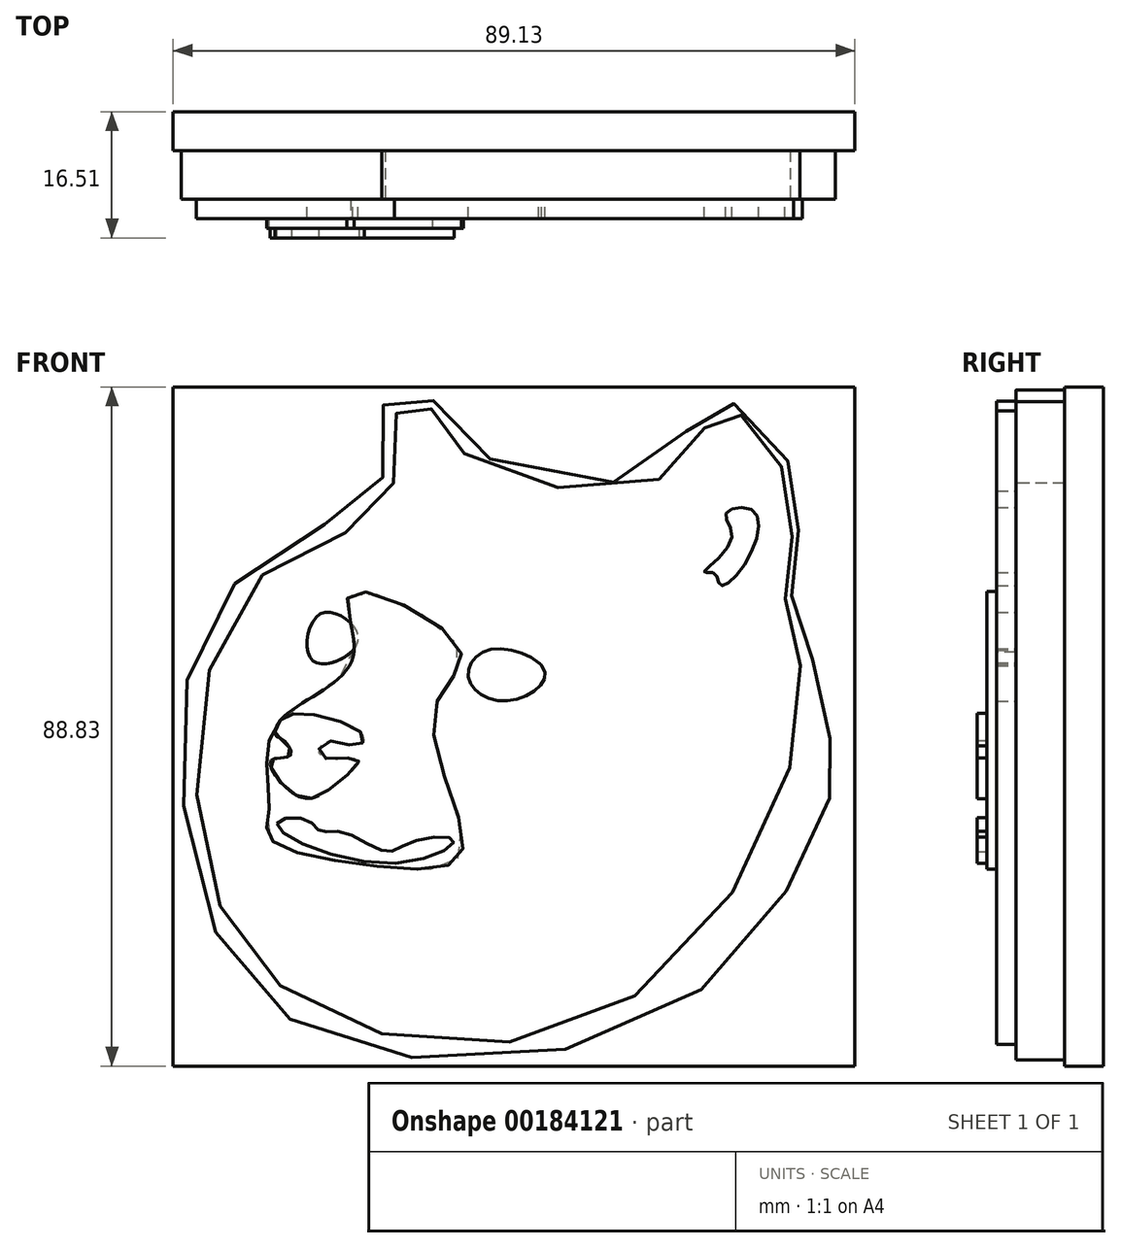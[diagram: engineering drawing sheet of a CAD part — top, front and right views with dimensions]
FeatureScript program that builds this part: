
annotation { "Feature Type Name" : "Feature", "Feature Type Description" : "" }
export const myFeature = defineFeature(function(context is Context, id is Id, definition is map)
    precondition{}
    {
        {
            var Q0;
            Q0=qCreatedBy(makeId("Front.planeOp"),FACE);
            var sketch = newSketch(context, id + "F0", { "sketchPlane" : qUnion([Q0])});
            skFitSpline(sketch, "E0", {"points": [v(14.94, 45.02) * mm, v(22.2, 53.36) * mm, v(26.38, 52.96) * mm, v(32.43, 41.52) * mm, v(31.36, 30.35) * mm, v(33.65, 16.35) * mm, v(11.17, -22.95) * mm, v(-29.47, -24.43) * mm, v(-44.95, -1.95) * mm, v(-37.01, 32.5) * mm, v(-20.6, 42.06) * mm, v(-19.11, 54.3) * mm, v(-15.34, 54.7) * mm, v(-10.63, 48.52) * mm, v(14.94, 45.02) * mm]});
            skFitSpline(sketch, "E1", {"points": [v(-29.31, 27.45) * mm, v(-24.63, 25.16) * mm, v(-26.06, 21.88) * mm, v(-30.59, 21.6) * mm, v(-29.31, 27.45) * mm]});
            skFitSpline(sketch, "E2", {"points": [v(-9.97, 18.96) * mm, v(-7.16, 22.78) * mm, v(0, 19.76) * mm, v(-4.88, 16.08) * mm, v(-9.97, 18.96) * mm]});
            skFitSpline(sketch, "E3", {"points": [v(23.71, 40.6) * mm, v(24.4, 37.2) * mm, v(20.85, 32.88) * mm, v(22.16, 32.77) * mm, v(22.95, 31.2) * mm, v(26.4, 34.37) * mm, v(27.23, 40.97) * mm, v(23.71, 40.6) * mm]});
            skFitSpline(sketch, "E4", {"points": [v(-0.44, 20.64) * mm, v(-3.05, 17.42) * mm, v(-6.06, 17.5) * mm, v(-6.22, 20.9) * mm, v(-2.1, 21.23) * mm, v(-0.44, 20.64) * mm]});
            skFitSpline(sketch, "E5", {"points": [v(-28.4, 26.53) * mm, v(-25.3, 26.14) * mm, v(-25.11, 22.7) * mm, v(-29.2, 21.88) * mm, v(-28.4, 26.53) * mm]});
            skSolve(sketch);
        }
        {
            var Q0;
            Q0 = qSketchRegion(id + "F0", true);
            extrude(context, id + "F1", {"entities" : qUnion([Q0]), "depth" : 2.54 * mm});
        }
        {
            var Q0;
            Q0=makeQuery(id+"F1.opExtrude","CAP_FACE",FACE,{"disambiguationData":[OSD([sQuery(id+"F0.wireOp",EDGE,"E0")])],"isStart":false});
            var sketch = newSketch(context, id + "F2", { "sketchPlane" : qUnion([Q0])});
            skFitSpline(sketch, "E6", {"points": [v(-25.34, 30.15) * mm, v(-25.05, 21.95) * mm, v(-34.17, 13.98) * mm, v(-36.35, 7.82) * mm, v(-36.09, 1.34) * mm, v(-35.95, -1.96) * mm, v(-21.33, -5.64) * mm, v(-10.78, -3.51) * mm, v(-14.57, 14.46) * mm, v(-11.11, 22.86) * mm, v(-25.34, 30.15) * mm]});
            skSolve(sketch);
        }
        {
            var Q0;
            Q0 = qSketchRegion(id + "F2", true);
            extrude(context, id + "F3", {"entities" : qUnion([Q0]), "operationType" : NewBodyOperationType.ADD, "depth" : 1.27 * mm});
        }
        {
            var Q0;
            Q0=makeQuery(id+"F3.opExtrude","CAP_FACE",FACE,{"disambiguationData":[OSD([sQuery(id+"F2.wireOp",EDGE,"E6")])],"isStart":false});
            var sketch = newSketch(context, id + "F4", { "sketchPlane" : qUnion([Q0])});
            skFitSpline(sketch, "E7", {"points": [v(-34.57, 13.58) * mm, v(-30.87, 14.33) * mm, v(-23.73, 11.57) * mm, v(-24.45, 10.24) * mm, v(-28.68, 10.71) * mm, v(-29.3, 8.76) * mm, v(-24.4, 8.47) * mm, v(-27.5, 5) * mm, v(-31.68, 3.38) * mm, v(-35.49, 6.71) * mm, v(-35.63, 8.43) * mm, v(-33.25, 8.95) * mm, v(-34.2, 10.95) * mm, v(-35.25, 11.66) * mm, v(-34.57, 13.58) * mm]});
            skFitSpline(sketch, "E8", {"points": [v(-35.02, 0) * mm, v(-31.25, 0.56) * mm, v(-29.39, -0.94) * mm, v(-26.57, -1.06) * mm, v(-20.82, -3.64) * mm, v(-17.58, -2.44) * mm, v(-11.94, -2.08) * mm, v(-20.22, -5.2) * mm, v(-35.02, 0) * mm]});
            skSolve(sketch);
        }
        {
            var Q0;
            Q0 = qSketchRegion(id + "F4", true);
            extrude(context, id + "F5", {"entities" : qUnion([Q0]), "operationType" : NewBodyOperationType.ADD, "depth" : 1.27 * mm});
        }
        {
            var Q0;
            Q0=qCreatedBy(makeId("Front.planeOp"),FACE);
            var sketch = newSketch(context, id + "F6", { "sketchPlane" : qUnion([Q0])});
            skFitSpline(sketch, "E9", {"points": [v(33.17, 38.4) * mm, v(32.14, 30.58) * mm, v(34.02, 25.11) * mm, v(36.75, 12.96) * mm, v(37.98, 7.69) * mm, v(34.5, -3.43) * mm, v(16.5, -24.35) * mm, v(-21.47, -30) * mm, v(-41.16, -17.66) * mm, v(-47.57, 9.76) * mm, v(-41.5, 30.4) * mm, v(-25.84, 40.77) * mm, v(-20.9, 46.6) * mm, v(-20.81, 55.45) * mm, v(-15.63, 56.2) * mm, v(-9.88, 49.42) * mm, v(12.92, 45.65) * mm, v(20.36, 53.94) * mm, v(25.07, 54.8) * mm, v(32.14, 46.69) * mm, v(33.17, 38.4) * mm]});
            skSolve(sketch);
        }
        {
            var Q0;
            Q0 = qSketchRegion(id + "F6", true);
            extrude(context, id + "F7", {"entities" : qUnion([Q0]), "operationType" : NewBodyOperationType.ADD, "oppositeDirection" : true, "depth" : 6.35 * mm});
        }
        {
            var Q0;
            Q0=makeQuery(id+"F7.opExtrude","CAP_FACE",FACE,{"disambiguationData":[OSD([sQuery(id+"F6.wireOp",EDGE,"E9")])],"isStart":false});
            var sketch = newSketch(context, id + "F8", { "sketchPlane" : qUnion([Q0])});
            skLineSegment(sketch, "E10.bottom", {"start": v(-40.53, -31.7) * mm, "end": v(48.6, -31.7) * mm});
            skLineSegment(sketch, "E10.top", {"start": v(-40.53, 57.13) * mm, "end": v(48.6, 57.13) * mm});
            skLineSegment(sketch, "E10.left", {"start": v(-40.53, -31.7) * mm, "end": v(-40.53, 57.13) * mm});
            skLineSegment(sketch, "E10.right", {"start": v(48.6, -31.7) * mm, "end": v(48.6, 57.13) * mm});
            skSolve(sketch);
        }
        {
            var Q0;
            Q0 = qSketchRegion(id + "F8", true);
            extrude(context, id + "F9", {"entities" : qUnion([Q0]), "operationType" : NewBodyOperationType.ADD, "depth" : 5.08 * mm});
        }
    });
